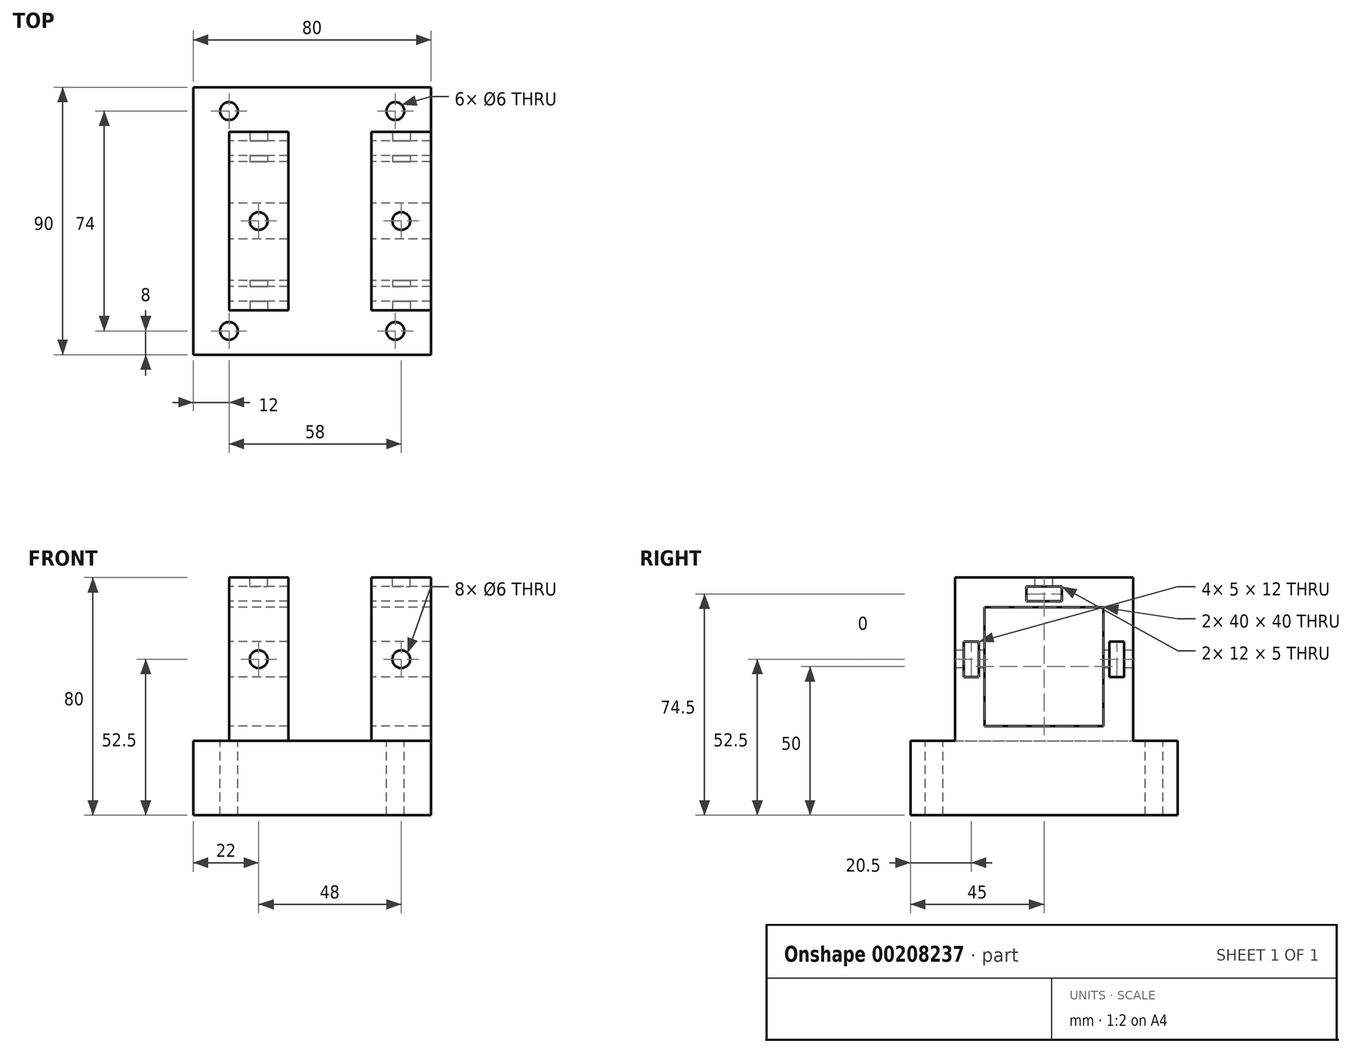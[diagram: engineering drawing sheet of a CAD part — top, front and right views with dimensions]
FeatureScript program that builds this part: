
annotation { "Feature Type Name" : "Feature", "Feature Type Description" : "" }
export const myFeature = defineFeature(function(context is Context, id is Id, definition is map)
    precondition{}
    {
        {
            var Q0;
            Q0=qCreatedBy(makeId("Right.planeOp"),FACE);
            var sketch = newSketch(context, id + "F0", { "sketchPlane" : qUnion([Q0])});
            skLineSegment(sketch, "E0.bottom", {"start": v(30, -40) * mm, "end": v(-30, -40) * mm});
            skLineSegment(sketch, "E0.top", {"start": v(30, 40) * mm, "end": v(-30, 40) * mm});
            skLineSegment(sketch, "E0.left", {"start": v(30, -40) * mm, "end": v(30, 40) * mm});
            skLineSegment(sketch, "E0.right", {"start": v(-30, -40) * mm, "end": v(-30, 40) * mm});
            skPoint(sketch, "E0.middle", {"position": v(0, 0) * mm});
            skSolve(sketch);
        }
        {
            var Q0;
            Q0 = qSketchRegion(id + "F0", true);
            extrude(context, id + "F1", {"entities" : qUnion([Q0]), "depth" : 20 * mm});
        }
        {
            var Q0;
            Q0=makeQuery(id+"F1.opExtrude","SWEPT_FACE",FACE,{"disambiguationData":[OSD([sQuery(id+"F0.wireOp",EDGE,"E0.bottom")])]});
            var sketch = newSketch(context, id + "F2", { "sketchPlane" : qUnion([Q0])});
            skLineSegment(sketch, "E1.bottom", {"start": v(20, 45) * mm, "end": v(-60, 45) * mm});
            skLineSegment(sketch, "E1.top", {"start": v(20, -45) * mm, "end": v(-60, -45) * mm});
            skLineSegment(sketch, "E1.left", {"start": v(20, 45) * mm, "end": v(20, -45) * mm});
            skLineSegment(sketch, "E1.right", {"start": v(-60, 45) * mm, "end": v(-60, -45) * mm});
            skLineSegment(sketch, "E2", {"start": v(20, 0) * mm, "end": v(0, 0) * mm, "construction": true});
            skSolve(sketch);
        }
        {
            var Q0;
            Q0 = qSketchRegion(id + "F2", true);
            extrude(context, id + "F3", {"entities" : qUnion([Q0]), "operationType" : NewBodyOperationType.ADD, "oppositeDirection" : true, "depth" : 25 * mm});
        }
        {
            var Q0;
            Q0=makeQuery(id+"F3.opExtrude","CAP_FACE",FACE,{"disambiguationData":[OSD([sQuery(id+"F2.wireOp",EDGE,"E1.bottom"),sQuery(id+"F2.wireOp",EDGE,"E1.top"),sQuery(id+"F2.wireOp",EDGE,"E1.left"),sQuery(id+"F2.wireOp",EDGE,"E1.right")])],"isStart":false});
            var sketch = newSketch(context, id + "F4", { "sketchPlane" : qUnion([Q0])});
            skLineSegment(sketch, "E3.bottom", {"start": v(-48, 37) * mm, "end": v(8, 37) * mm, "construction": true});
            skLineSegment(sketch, "E3.top", {"start": v(-48, -37) * mm, "end": v(8, -37) * mm, "construction": true});
            skLineSegment(sketch, "E3.left", {"start": v(-48, 37) * mm, "end": v(-48, -37) * mm, "construction": true});
            skLineSegment(sketch, "E3.right", {"start": v(8, 37) * mm, "end": v(8, -37) * mm, "construction": true});
            skLineSegment(sketch, "E4", {"start": v(8, 0) * mm, "end": v(0, 0) * mm, "construction": true});
            skCircle(sketch, "E5", {"center": v(-48, 37) * mm, "radius": 3 * mm});
            skCircle(sketch, "E6", {"center": v(-48, -37) * mm, "radius": 3 * mm});
            skCircle(sketch, "E7", {"center": v(8, -37) * mm, "radius": 3 * mm});
            skCircle(sketch, "E8", {"center": v(8, 37) * mm, "radius": 3 * mm});
            skSolve(sketch);
        }
        {
            var Q0;
            Q0 = qSketchRegion(id + "F4", true);
            extrude(context, id + "F5", {"entities" : qUnion([Q0]), "operationType" : NewBodyOperationType.REMOVE, "endBound" : BoundingType.THROUGH_ALL, "oppositeDirection" : true, "depth" : 25 * mm});
        }
        {
            var Q0;
            Q0=makeQuery(id+"F3.opExtrude","CAP_FACE",FACE,{"disambiguationData":[OSD([sQuery(id+"F2.wireOp",EDGE,"E1.bottom"),sQuery(id+"F2.wireOp",EDGE,"E1.top"),sQuery(id+"F2.wireOp",EDGE,"E1.left"),sQuery(id+"F2.wireOp",EDGE,"E1.right")])],"isStart":false});
            var sketch = newSketch(context, id + "F6", { "sketchPlane" : qUnion([Q0])});
            skLineSegment(sketch, "E9.bottom", {"start": v(-48, 30) * mm, "end": v(-28, 30) * mm});
            skLineSegment(sketch, "E9.top", {"start": v(-48, -30) * mm, "end": v(-28, -30) * mm});
            skLineSegment(sketch, "E9.left", {"start": v(-48, 30) * mm, "end": v(-48, -30) * mm});
            skLineSegment(sketch, "E9.right", {"start": v(-28, 30) * mm, "end": v(-28, -30) * mm});
            skLineSegment(sketch, "E10", {"start": v(-48, 0) * mm, "end": v(-60, 0) * mm, "construction": true});
            skPoint(sketch, "E10.endSnap0", {"position": v(-60, 0) * mm});
            skSolve(sketch);
        }
        {
            var Q0;
            Q0 = qSketchRegion(id + "F6", true);
            var Q1;
            Q1=makeQuery(id+"F1.opExtrude","SWEPT_FACE",FACE,{"disambiguationData":[OSD([sQuery(id+"F0.wireOp",EDGE,"E0.top")])]});
            extrude(context, id + "F7", {"entities" : qUnion([Q0]), "operationType" : NewBodyOperationType.ADD, "endBound" : BoundingType.UP_TO_SURFACE, "endBoundEntityFace" : qUnion([Q1]), "depth" : 25 * mm});
        }
        {
            var Q0;
            Q0=makeQuery(id+"F7.opExtrude","SWEPT_FACE",FACE,{"disambiguationData":[OSD([sQuery(id+"F6.wireOp",EDGE,"E9.left")])]});
            var sketch = newSketch(context, id + "F8", { "sketchPlane" : qUnion([Q0])});
            skLineSegment(sketch, "E11.bottom", {"start": v(-20, -10) * mm, "end": v(20, -10) * mm});
            skLineSegment(sketch, "E11.top", {"start": v(-20, 30) * mm, "end": v(20, 30) * mm});
            skLineSegment(sketch, "E11.left", {"start": v(-20, -10) * mm, "end": v(-20, 30) * mm});
            skLineSegment(sketch, "E11.right", {"start": v(20, -10) * mm, "end": v(20, 30) * mm});
            skLineSegment(sketch, "E12.bottom", {"start": v(-27, 6.5) * mm, "end": v(-22, 6.5) * mm});
            skLineSegment(sketch, "E12.top", {"start": v(-27, 18.5) * mm, "end": v(-22, 18.5) * mm});
            skLineSegment(sketch, "E12.left", {"start": v(-27, 6.5) * mm, "end": v(-27, 18.5) * mm});
            skLineSegment(sketch, "E12.right", {"start": v(-22, 6.5) * mm, "end": v(-22, 18.5) * mm});
            skPoint(sketch, "E13.middle.positionSnap0", {"position": v(20, 10) * mm});
            skLineSegment(sketch, "E14.bottom", {"start": v(-6, 37) * mm, "end": v(6, 37) * mm});
            skLineSegment(sketch, "E14.top", {"start": v(-6, 32) * mm, "end": v(6, 32) * mm});
            skLineSegment(sketch, "E14.left", {"start": v(-6, 37) * mm, "end": v(-6, 32) * mm});
            skLineSegment(sketch, "E14.right", {"start": v(6, 37) * mm, "end": v(6, 32) * mm});
            skPoint(sketch, "E14.middle", {"position": v(0, 34.5) * mm});
            skLineSegment(sketch, "E15", {"start": v(0, 37) * mm, "end": v(0, 40) * mm, "construction": true});
            skLineSegment(sketch, "E16", {"start": v(0, 34.5) * mm, "end": v(0, 10) * mm, "construction": true});
            skPoint(sketch, "E16.endSnap0", {"position": v(0, 30) * mm});
            skLineSegment(sketch, "E17", {"start": v(0, 10) * mm, "end": v(-20, 10) * mm, "construction": true});
            skLineSegment(sketch, "E18", {"start": v(-30, 12.5) * mm, "end": v(-27, 12.5) * mm, "construction": true});
            skLineSegment(sketch, "E19.MirrorCS", {"start": v(27, 18.5) * mm, "end": v(22, 18.5) * mm});
            skLineSegment(sketch, "E20.MirrorCS", {"start": v(22, 6.5) * mm, "end": v(22, 18.5) * mm});
            skLineSegment(sketch, "E21.MirrorCS", {"start": v(27, 6.5) * mm, "end": v(27, 18.5) * mm});
            skLineSegment(sketch, "E22.MirrorCS", {"start": v(27, 6.5) * mm, "end": v(22, 6.5) * mm});
            skLineSegment(sketch, "E23.MirrorCS", {"start": v(30, 12.5) * mm, "end": v(27, 12.5) * mm, "construction": true});
            skSolve(sketch);
        }
        {
            var Q0;
            Q0 = qSketchRegion(id + "F8", true);
            extrude(context, id + "F9", {"entities" : qUnion([Q0]), "operationType" : NewBodyOperationType.REMOVE, "endBound" : BoundingType.THROUGH_ALL, "oppositeDirection" : true, "depth" : 25 * mm});
        }
        {
            var Q0;
            Q0=makeQuery(id+"F7.opExtrude","SWEPT_FACE",FACE,{"disambiguationData":[OSD([sQuery(id+"F6.wireOp",EDGE,"E9.top")])]});
            var sketch = newSketch(context, id + "F10", { "sketchPlane" : qUnion([Q0])});
            skLineSegment(sketch, "E24", {"start": v(-48, 12.5) * mm, "end": v(-28, 12.5) * mm, "construction": true});
            skLineSegment(sketch, "E25", {"start": v(0, 12.5) * mm, "end": v(20, 12.5) * mm, "construction": true});
            skCircle(sketch, "E26", {"center": v(-38, 12.5) * mm, "radius": 3 * mm});
            skCircle(sketch, "E27", {"center": v(10, 12.5) * mm, "radius": 3 * mm});
            skSolve(sketch);
        }
        {
            var Q0;
            Q0 = qSketchRegion(id + "F10", true);
            extrude(context, id + "F11", {"entities" : qUnion([Q0]), "operationType" : NewBodyOperationType.REMOVE, "endBound" : BoundingType.THROUGH_ALL, "oppositeDirection" : true, "depth" : 25 * mm});
        }
        {
            var Q0;
            Q0=makeQuery(id+"F7.opExtrude","CAP_FACE",FACE,{"disambiguationData":[OSD([sQuery(id+"F6.wireOp",EDGE,"E9.bottom"),sQuery(id+"F6.wireOp",EDGE,"E9.top"),sQuery(id+"F6.wireOp",EDGE,"E9.left"),sQuery(id+"F6.wireOp",EDGE,"E9.right")])],"isStart":false});
            var sketch = newSketch(context, id + "F12", { "sketchPlane" : qUnion([Q0])});
            skLineSegment(sketch, "E28", {"start": v(-48, 0) * mm, "end": v(-28, 0) * mm, "construction": true});
            skLineSegment(sketch, "E29", {"start": v(0, 0) * mm, "end": v(20, 0) * mm, "construction": true});
            skCircle(sketch, "E30", {"center": v(-38, 0) * mm, "radius": 3 * mm});
            skCircle(sketch, "E31", {"center": v(10, 0) * mm, "radius": 3 * mm});
            skSolve(sketch);
        }
        {
            var Q0;
            Q0 = qSketchRegion(id + "F12", true);
            extrude(context, id + "F13", {"entities" : qUnion([Q0]), "operationType" : NewBodyOperationType.REMOVE, "endBound" : BoundingType.UP_TO_NEXT, "oppositeDirection" : true, "depth" : 25 * mm});
        }
    });
